# Revit family: Parex_SpecialityEquipment_Giulia_Rangehood
name_source: partatom
category: Specialty Equipment
units: mm (PartAtom-declared; Revit-internal decimal feet)

## family parameters
Always vertical = Yes
Cut with Voids When Loaded = No
Enable Cutting in Views = Yes
Maintain Annotation Orientation = No
Part Type = Normal
Room Calculation Point = No
Round Connector Dimension = Use Diameter
Shared = No
Work Plane-Based = No

## types (1)
- Parex_SpecialityEquipment_Giulia_Rangehood
    Calc_FrameOffset = 10 mm  [stored 0.0328084 ft]
    Calc_RearFrameWidth = 90 mm  [stored 0.295276 ft]
    ChimneyDepth = 290 mm  [stored 0.951444 ft]
    ChimneyWidth = 315 mm  [stored 1.03346 ft]
    Default Elevation = 1000 mm  [stored 3.28084 ft]
    Depth = 500 mm  [stored 1.64042 ft]
    Description = The Giulia 900mm wall-mounted rangehood is suitable for up to a 900mm cooktop. With angled sleek lines it will fit into you kitchen seemlessly and can be paired with  a  motor to suit your cooking requirements.
    Export Type to IFC As = IfcElectricApplianceType
    FilterMaterial = Parex_Metal_Filter
    Height = 1000 mm  [stored 3.28084 ft]
    HeightOffset = 111 mm
    HoodThickness = 30 mm  [stored 0.0984252 ft]
    Manufacturer = Amore Homes
    Material = Parex_Metal_430 Stainless Steel
    Model = Giulia 900mm Wall-Mount Rangehood
    MountType = Wall-Mount
    Specifications = Quiet operation with external motor
Expel smoke, grease, smells & steam outside
Easy control with soft touch eye level controls
Great control with 5-speed levels
15-Minute delay timer with auto shut-off
Twin LED lights gives you great stove top lighting
Sturdy hood made of 1mm 430 stainless steel
Stainless steel dishwasher safe filters
Remote control for optimum convenience
Dimensions: 900mm wide x 500mm deep
Includes 5m ducting
    Type IFC Predefined Type = NOTDEFINED
    URL = https://amorehomes.co.nz
    WarrantyDescription = 5-Year in-home warranty on hood, 10-Year in-home warranty on motor
    Width = 900 mm  [stored 2.95276 ft]

note: [stored X ft] marks values corroborated as IEEE doubles in the binary element streams (Revit-internal decimal feet)

## geometry (parser evidence)
native form markers: Sweep x7
no freeform markers — native parametric forms only
